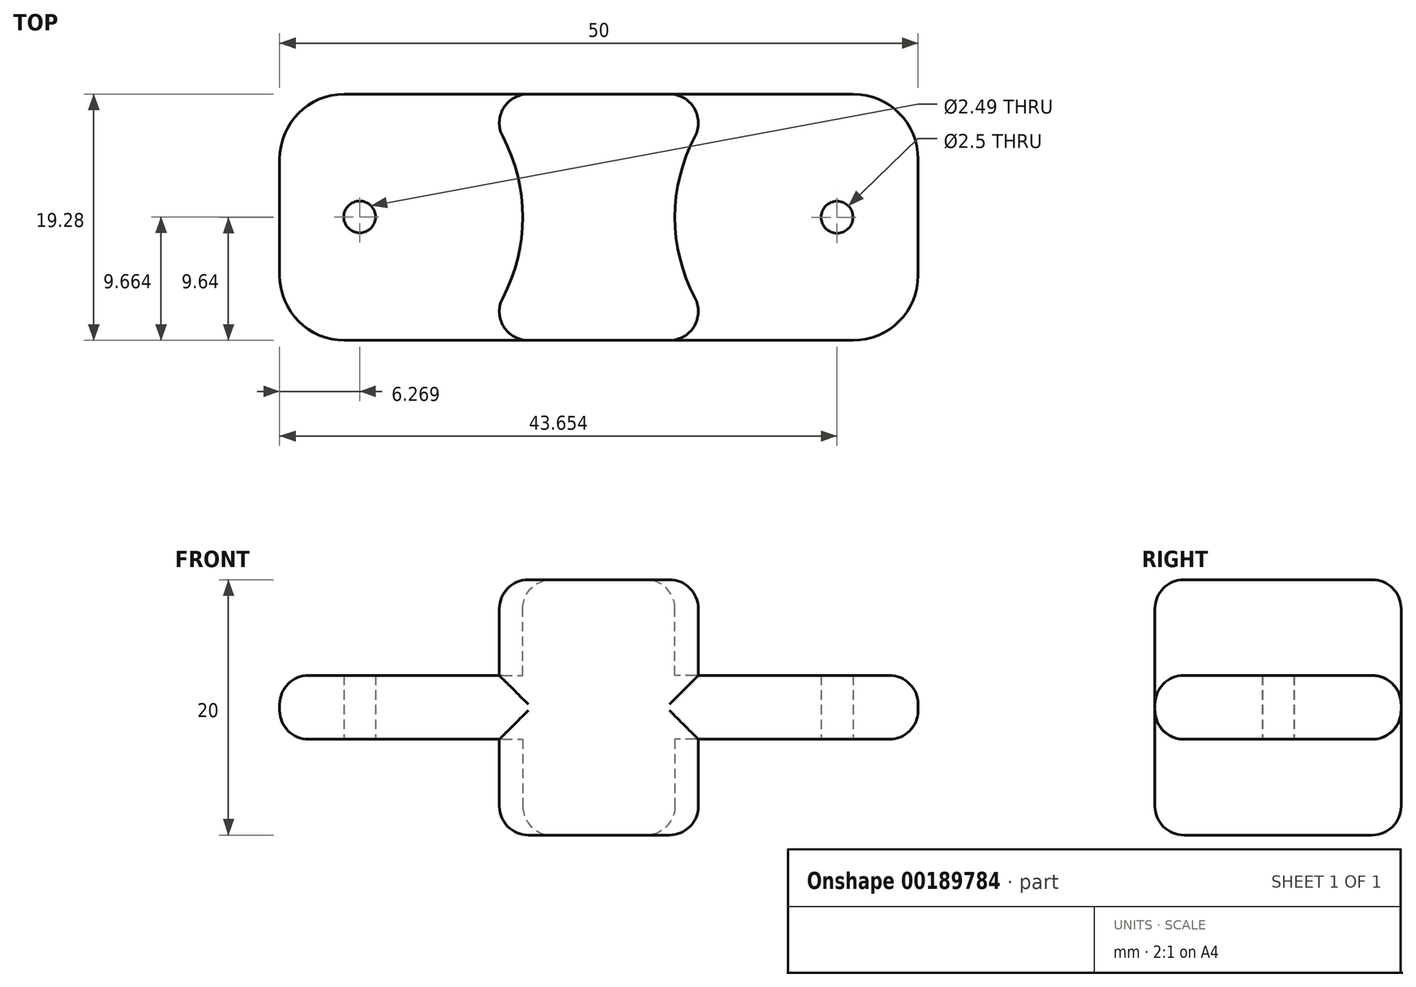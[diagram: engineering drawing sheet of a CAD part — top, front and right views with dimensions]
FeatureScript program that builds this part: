
annotation { "Feature Type Name" : "Feature", "Feature Type Description" : "" }
export const myFeature = defineFeature(function(context is Context, id is Id, definition is map)
    precondition{}
    {
        {
            var Q0;
            Q0=qCreatedBy(makeId("Top.planeOp"),FACE);
            var sketch = newSketch(context, id + "F0", { "sketchPlane" : qUnion([Q0])});
            skLineSegment(sketch, "E0", {"start": v(0, 0) * mm, "end": v(-10, 0) * mm});
            skLineSegment(sketch, "E1", {"start": v(-10, 19.28) * mm, "end": v(0, 19.28) * mm});
            skLineSegment(sketch, "E2", {"start": v(0, 19.28) * mm, "end": v(10, 19.28) * mm});
            skLineSegment(sketch, "E3", {"start": v(10, 0) * mm, "end": v(0, 0) * mm});
            skLineSegment(sketch, "E4", {"start": v(-10, 19.28) * mm, "end": v(-19.92, 19.28) * mm});
            skLineSegment(sketch, "E5", {"start": v(-25, 14.2) * mm, "end": v(-25, 5.08) * mm});
            skLineSegment(sketch, "E6", {"start": v(-19.92, 0) * mm, "end": v(-10, 0) * mm});
            skLineSegment(sketch, "E7.bottom", {"start": v(10, 19.28) * mm, "end": v(19.92, 19.28) * mm});
            skLineSegment(sketch, "E7.top", {"start": v(10, 0) * mm, "end": v(19.92, 0) * mm});
            skLineSegment(sketch, "E7.right", {"start": v(25, 14.2) * mm, "end": v(25, 5.08) * mm});
            skLineSegment(sketch, "E8", {"start": v(-17.5, 19.28) * mm, "end": v(-17.5, 0) * mm, "construction": true});
            skLineSegment(sketch, "E9", {"start": v(17.5, 19.28) * mm, "end": v(17.5, 0) * mm, "construction": true});
            skCircle(sketch, "E10", {"center": v(-18.73, 9.66) * mm, "radius": 1.24 * mm});
            skCircle(sketch, "E11", {"center": v(18.65, 9.64) * mm, "radius": 1.25 * mm});
            skLineSegment(sketch, "E12", {"start": v(-25, 9.64) * mm, "end": v(-18.73, 9.66) * mm});
            skLineSegment(sketch, "E13", {"start": v(-25, 9.64) * mm, "end": v(-18.73, 9.66) * mm, "construction": true});
            skLineSegment(sketch, "E14", {"start": v(-10, 0) * mm, "end": v(10, 0) * mm, "construction": true});
            skLineSegment(sketch, "E15", {"start": v(-10, 19.28) * mm, "end": v(0, 19.28) * mm, "construction": true});
            skPoint(sketch, "E16.visualSharp", {"position": v(-25, 19.28) * mm});
            skArc(sketch, "E16.filletArc", {"start": v(-19.92, 19.28) * mm, "mid": v(-23.51, 17.8) * mm, "end": v(-25, 14.2) * mm});
            skPoint(sketch, "E17.visualSharp", {"position": v(-25, 0) * mm});
            skArc(sketch, "E17.filletArc", {"start": v(-25, 5.08) * mm, "mid": v(-23.51, 1.49) * mm, "end": v(-19.92, 0) * mm});
            skPoint(sketch, "E18.visualSharp", {"position": v(25, 19.28) * mm});
            skArc(sketch, "E18.filletArc", {"start": v(25, 14.2) * mm, "mid": v(23.51, 17.8) * mm, "end": v(19.92, 19.28) * mm});
            skPoint(sketch, "E19.visualSharp", {"position": v(25, 0) * mm});
            skArc(sketch, "E19.filletArc", {"start": v(19.92, 0) * mm, "mid": v(23.51, 1.49) * mm, "end": v(25, 5.08) * mm});
            skLineSegment(sketch, "E20.bottom", {"start": v(-10, 19.28) * mm, "end": v(10, 19.28) * mm});
            skLineSegment(sketch, "E20.top", {"start": v(-10, 0) * mm, "end": v(10, 0) * mm});
            skArc(sketch, "E21", {"start": v(-10, 0) * mm, "mid": v(-5.7, 9.64) * mm, "end": v(-10, 19.28) * mm});
            skArc(sketch, "E22", {"start": v(10, 19.28) * mm, "mid": v(5.7, 9.64) * mm, "end": v(10, 0) * mm});
            skSolve(sketch);
        }
        {
            var Q0;
            {var subQ0=sQuery(id+"F0.wireOp",EDGE,"E21");Q0=makeQuery(id+"F0.imprint","IMPRINT",FACE,{"disambiguationData":[TD([[makeQuery(id+"F0.imprint","IMPRINT",EDGE,{"derivedFrom":subQ0}),-1.0]])]});}
            var Q1;
            Q1=makeQuery(id+"F0.imprint","IMPRINT",FACE,{"disambiguationData":[TD([[makeQuery(id+"F0.imprint","IMPRINT",EDGE,{"derivedFrom":sQuery(id+"F0.wireOp",EDGE,"E4")}),1.0]])]});
            var Q2;
            Q2=makeQuery(id+"F0.imprint","IMPRINT",FACE,{"disambiguationData":[TD([[makeQuery(id+"F0.imprint","IMPRINT",EDGE,{"derivedFrom":sQuery(id+"F0.wireOp",EDGE,"E7.bottom")}),-1.0]])]});
            extrude(context, id + "F1", {"entities" : qUnion([Q0, Q1, Q2]), "depth" : 20 * mm});
        }
        {
            var Q0;
            Q0=qCreatedBy(makeId("Front.planeOp"),FACE);
            var sketch = newSketch(context, id + "F2", { "sketchPlane" : qUnion([Q0])});
            skLineSegment(sketch, "E23.bottom", {"start": v(0, 0) * mm, "end": v(-10, 0) * mm});
            skLineSegment(sketch, "E23.top", {"start": v(0, 20) * mm, "end": v(-10, 20) * mm});
            skLineSegment(sketch, "E23.right", {"start": v(-10, 0) * mm, "end": v(-10, 7.5) * mm});
            skLineSegment(sketch, "E24.bottom", {"start": v(0, 20) * mm, "end": v(10, 20) * mm});
            skLineSegment(sketch, "E24.top", {"start": v(0, 0) * mm, "end": v(10, 0) * mm});
            skLineSegment(sketch, "E24.right", {"start": v(10, 20) * mm, "end": v(10, 12.5) * mm});
            skLineSegment(sketch, "E25", {"start": v(-25, 7.5) * mm, "end": v(-25, 10) * mm});
            skLineSegment(sketch, "E26", {"start": v(-25, 7.5) * mm, "end": v(-10, 7.5) * mm});
            skLineSegment(sketch, "E27", {"start": v(-25, 10) * mm, "end": v(-25, 12.5) * mm});
            skLineSegment(sketch, "E28", {"start": v(-25, 7.5) * mm, "end": v(-25, 12.5) * mm});
            skLineSegment(sketch, "E29.top", {"start": v(10, 12.5) * mm, "end": v(25, 12.5) * mm});
            skLineSegment(sketch, "E29.right", {"start": v(25, 10) * mm, "end": v(25, 12.5) * mm});
            skLineSegment(sketch, "E30.top", {"start": v(10, 7.5) * mm, "end": v(25, 7.5) * mm});
            skLineSegment(sketch, "E30.right", {"start": v(25, 10) * mm, "end": v(25, 7.5) * mm});
            skLineSegment(sketch, "E31.trimOffspring", {"start": v(10, 7.5) * mm, "end": v(10, 0) * mm});
            skLineSegment(sketch, "E32", {"start": v(-25, 12.5) * mm, "end": v(-10, 12.5) * mm});
            skLineSegment(sketch, "E33", {"start": v(-10, 20) * mm, "end": v(-10, 12.5) * mm});
            skLineSegment(sketch, "E34", {"start": v(-10, 0) * mm, "end": v(10, 0) * mm});
            skSolve(sketch);
        }
        {
            var Q0;
            Q0=makeQuery(id+"F2.imprint","IMPRINT",FACE,{"disambiguationData":[TD([[makeQuery(id+"F2.imprint","IMPRINT",EDGE,{"derivedFrom":sQuery(id+"F2.wireOp",EDGE,"E23.top")}),1.0]])]});
            extrude(context, id + "F3", {"entities" : qUnion([Q0]), "operationType" : NewBodyOperationType.INTERSECT, "oppositeDirection" : true, "depth" : 20 * mm});
        }
        {
            var Q0;
            Q0=makeQuery(id+"F1.opExtrude","CAP_FACE",FACE,{"disambiguationData":[OSD([sQuery(id+"F0.wireOp",EDGE,"E4"),sQuery(id+"F0.wireOp",EDGE,"E5"),sQuery(id+"F0.wireOp",EDGE,"E6"),sQuery(id+"F0.wireOp",EDGE,"E7.bottom"),sQuery(id+"F0.wireOp",EDGE,"E7.top"),sQuery(id+"F0.wireOp",EDGE,"E7.right"),sQuery(id+"F0.wireOp",EDGE,"E10"),sQuery(id+"F0.wireOp",EDGE,"E11"),sQuery(id+"F0.wireOp",EDGE,"E16.filletArc"),sQuery(id+"F0.wireOp",EDGE,"E17.filletArc"),sQuery(id+"F0.wireOp",EDGE,"E18.filletArc"),sQuery(id+"F0.wireOp",EDGE,"E19.filletArc"),sQuery(id+"F0.wireOp",EDGE,"E20.bottom"),sQuery(id+"F0.wireOp",EDGE,"E20.top")])],"isStart":false});
            var sketch = newSketch(context, id + "F4", { "sketchPlane" : qUnion([Q0])});
            skLineSegment(sketch, "E35.left", {"start": v(-10, 19.28) * mm, "end": v(-10, 0) * mm});
            skLineSegment(sketch, "E35.right", {"start": v(-6, 10.68) * mm, "end": v(-6, 8.6) * mm});
            skLineSegment(sketch, "E36.left", {"start": v(10, 19.28) * mm, "end": v(10, 0) * mm});
            skLineSegment(sketch, "E36.right", {"start": v(6, 10.73) * mm, "end": v(6, 8.55) * mm});
            skArc(sketch, "E37", {"start": v(-10, 0) * mm, "mid": v(-5.96, 9.64) * mm, "end": v(-10, 19.28) * mm});
            skArc(sketch, "E38", {"start": v(10, 19.28) * mm, "mid": v(5.96, 9.64) * mm, "end": v(10, 0) * mm});
            skSolve(sketch);
        }
        {
            var Q0;
            Q0 = qSketchRegion(id + "F4", true);
            extrude(context, id + "F5", {"entities" : qUnion([Q0]), "operationType" : NewBodyOperationType.REMOVE, "oppositeDirection" : true, "depth" : 7.5 * mm});
        }
        {
            var Q0;
            Q0=makeQuery(id+"F1.opExtrude","CAP_FACE",FACE,{"disambiguationData":[OSD([sQuery(id+"F0.wireOp",EDGE,"E4"),sQuery(id+"F0.wireOp",EDGE,"E5"),sQuery(id+"F0.wireOp",EDGE,"E6"),sQuery(id+"F0.wireOp",EDGE,"E7.bottom"),sQuery(id+"F0.wireOp",EDGE,"E7.top"),sQuery(id+"F0.wireOp",EDGE,"E7.right"),sQuery(id+"F0.wireOp",EDGE,"E10"),sQuery(id+"F0.wireOp",EDGE,"E11"),sQuery(id+"F0.wireOp",EDGE,"E16.filletArc"),sQuery(id+"F0.wireOp",EDGE,"E17.filletArc"),sQuery(id+"F0.wireOp",EDGE,"E18.filletArc"),sQuery(id+"F0.wireOp",EDGE,"E19.filletArc"),sQuery(id+"F0.wireOp",EDGE,"E20.bottom"),sQuery(id+"F0.wireOp",EDGE,"E20.top")])],"isStart":true});
            var sketch = newSketch(context, id + "F6", { "sketchPlane" : qUnion([Q0])});
            skLineSegment(sketch, "E39", {"start": v(-10, 0) * mm, "end": v(-10, -19.28) * mm});
            skLineSegment(sketch, "E40", {"start": v(10, 0) * mm, "end": v(10, -19.28) * mm});
            skArc(sketch, "E41", {"start": v(-10, -19.28) * mm, "mid": v(-5.96, -9.64) * mm, "end": v(-10, 0) * mm});
            skArc(sketch, "E42", {"start": v(10, 0) * mm, "mid": v(5.96, -9.64) * mm, "end": v(10, -19.28) * mm});
            skSolve(sketch);
        }
        {
            var Q0;
            Q0 = qSketchRegion(id + "F6", true);
            extrude(context, id + "F7", {"entities" : qUnion([Q0]), "operationType" : NewBodyOperationType.REMOVE, "oppositeDirection" : true, "depth" : 7.5 * mm});
        }
        {
            var Q0;
            Q0=makeQuery(id+"F1.opExtrude","SWEPT_FACE",FACE,{"disambiguationData":[OSD([sQuery(id+"F0.wireOp",EDGE,"E6"),sQuery(id+"F0.wireOp",EDGE,"E7.top"),sQuery(id+"F0.wireOp",EDGE,"E20.top")])]});
            var Q1;
            Q1=makeQuery(id+"F1.opExtrude","CAP_FACE",FACE,{"disambiguationData":[OSD([sQuery(id+"F0.wireOp",EDGE,"E4"),sQuery(id+"F0.wireOp",EDGE,"E5"),sQuery(id+"F0.wireOp",EDGE,"E6"),sQuery(id+"F0.wireOp",EDGE,"E7.bottom"),sQuery(id+"F0.wireOp",EDGE,"E7.top"),sQuery(id+"F0.wireOp",EDGE,"E7.right"),sQuery(id+"F0.wireOp",EDGE,"E10"),sQuery(id+"F0.wireOp",EDGE,"E11"),sQuery(id+"F0.wireOp",EDGE,"E16.filletArc"),sQuery(id+"F0.wireOp",EDGE,"E17.filletArc"),sQuery(id+"F0.wireOp",EDGE,"E18.filletArc"),sQuery(id+"F0.wireOp",EDGE,"E19.filletArc"),sQuery(id+"F0.wireOp",EDGE,"E20.bottom"),sQuery(id+"F0.wireOp",EDGE,"E20.top")])],"isStart":true});
            var Q2;
            Q2=makeQuery(id+"F7.boolean.opBoolean","MERGE",FACE,{"derivedFrom":[makeQuery(id+"F3.boolean.opBoolean","COPY",FACE,{"derivedFrom":makeQuery(id+"F3.boolean.toolComplement.opBoolean","COPY",FACE,{"derivedFrom":makeQuery(id+"F3.opExtrude","SWEPT_FACE",FACE,{"disambiguationData":[OSD([sQuery(id+"F2.wireOp",EDGE,"E26")])]})})}),makeQuery(id+"F7.opExtrude","CAP_FACE",FACE,{"disambiguationData":[OSD([sQuery(id+"F6.wireOp",EDGE,"E39"),sQuery(id+"F6.wireOp",EDGE,"E41")])],"isStart":false})]});
            var Q3;
            Q3=makeQuery(id+"F7.boolean.opBoolean","MERGE",FACE,{"derivedFrom":[makeQuery(id+"F3.boolean.opBoolean","COPY",FACE,{"derivedFrom":makeQuery(id+"F3.boolean.toolComplement.opBoolean","COPY",FACE,{"derivedFrom":makeQuery(id+"F3.opExtrude","SWEPT_FACE",FACE,{"disambiguationData":[OSD([sQuery(id+"F2.wireOp",EDGE,"E30.top")])]})})}),makeQuery(id+"F7.opExtrude","CAP_FACE",FACE,{"disambiguationData":[OSD([sQuery(id+"F6.wireOp",EDGE,"E40"),sQuery(id+"F6.wireOp",EDGE,"E42")])],"isStart":false})]});
            var Q4;
            Q4=makeQuery(id+"F1.opExtrude","SWEPT_FACE",FACE,{"disambiguationData":[OSD([sQuery(id+"F0.wireOp",EDGE,"E4"),sQuery(id+"F0.wireOp",EDGE,"E7.bottom"),sQuery(id+"F0.wireOp",EDGE,"E20.bottom")])]});
            var Q5;
            Q5=makeQuery(id+"F1.opExtrude","CAP_FACE",FACE,{"disambiguationData":[OSD([sQuery(id+"F0.wireOp",EDGE,"E4"),sQuery(id+"F0.wireOp",EDGE,"E5"),sQuery(id+"F0.wireOp",EDGE,"E6"),sQuery(id+"F0.wireOp",EDGE,"E7.bottom"),sQuery(id+"F0.wireOp",EDGE,"E7.top"),sQuery(id+"F0.wireOp",EDGE,"E7.right"),sQuery(id+"F0.wireOp",EDGE,"E10"),sQuery(id+"F0.wireOp",EDGE,"E11"),sQuery(id+"F0.wireOp",EDGE,"E16.filletArc"),sQuery(id+"F0.wireOp",EDGE,"E17.filletArc"),sQuery(id+"F0.wireOp",EDGE,"E18.filletArc"),sQuery(id+"F0.wireOp",EDGE,"E19.filletArc"),sQuery(id+"F0.wireOp",EDGE,"E20.bottom"),sQuery(id+"F0.wireOp",EDGE,"E20.top")])],"isStart":false});
            var Q6;
            Q6=makeQuery(id+"F5.boolean.opBoolean","MERGE",FACE,{"derivedFrom":[makeQuery(id+"F3.boolean.opBoolean","COPY",FACE,{"derivedFrom":makeQuery(id+"F3.boolean.toolComplement.opBoolean","COPY",FACE,{"derivedFrom":makeQuery(id+"F3.opExtrude","SWEPT_FACE",FACE,{"disambiguationData":[OSD([sQuery(id+"F2.wireOp",EDGE,"E32")])]})})}),makeQuery(id+"F5.opExtrude","CAP_FACE",FACE,{"disambiguationData":[OSD([sQuery(id+"F4.wireOp",EDGE,"E35.left"),sQuery(id+"F4.wireOp",EDGE,"E37")])],"isStart":false})]});
            var Q7;
            Q7=makeQuery(id+"F5.boolean.opBoolean","MERGE",FACE,{"derivedFrom":[makeQuery(id+"F3.boolean.opBoolean","COPY",FACE,{"derivedFrom":makeQuery(id+"F3.boolean.toolComplement.opBoolean","COPY",FACE,{"derivedFrom":makeQuery(id+"F3.opExtrude","SWEPT_FACE",FACE,{"disambiguationData":[OSD([sQuery(id+"F2.wireOp",EDGE,"E29.top")])]})})}),makeQuery(id+"F5.opExtrude","CAP_FACE",FACE,{"disambiguationData":[OSD([sQuery(id+"F4.wireOp",EDGE,"E36.left"),sQuery(id+"F4.wireOp",EDGE,"E38")])],"isStart":false})]});
            fillet(context, id + "F8", {"entities" : qUnion([Q0, Q1, Q2, Q3, Q4, Q5, Q6, Q7]), "radius" : 2.26 * mm, "tangentPropagation" : true, "allowEdgeOverflow" : false});
        }
    });
